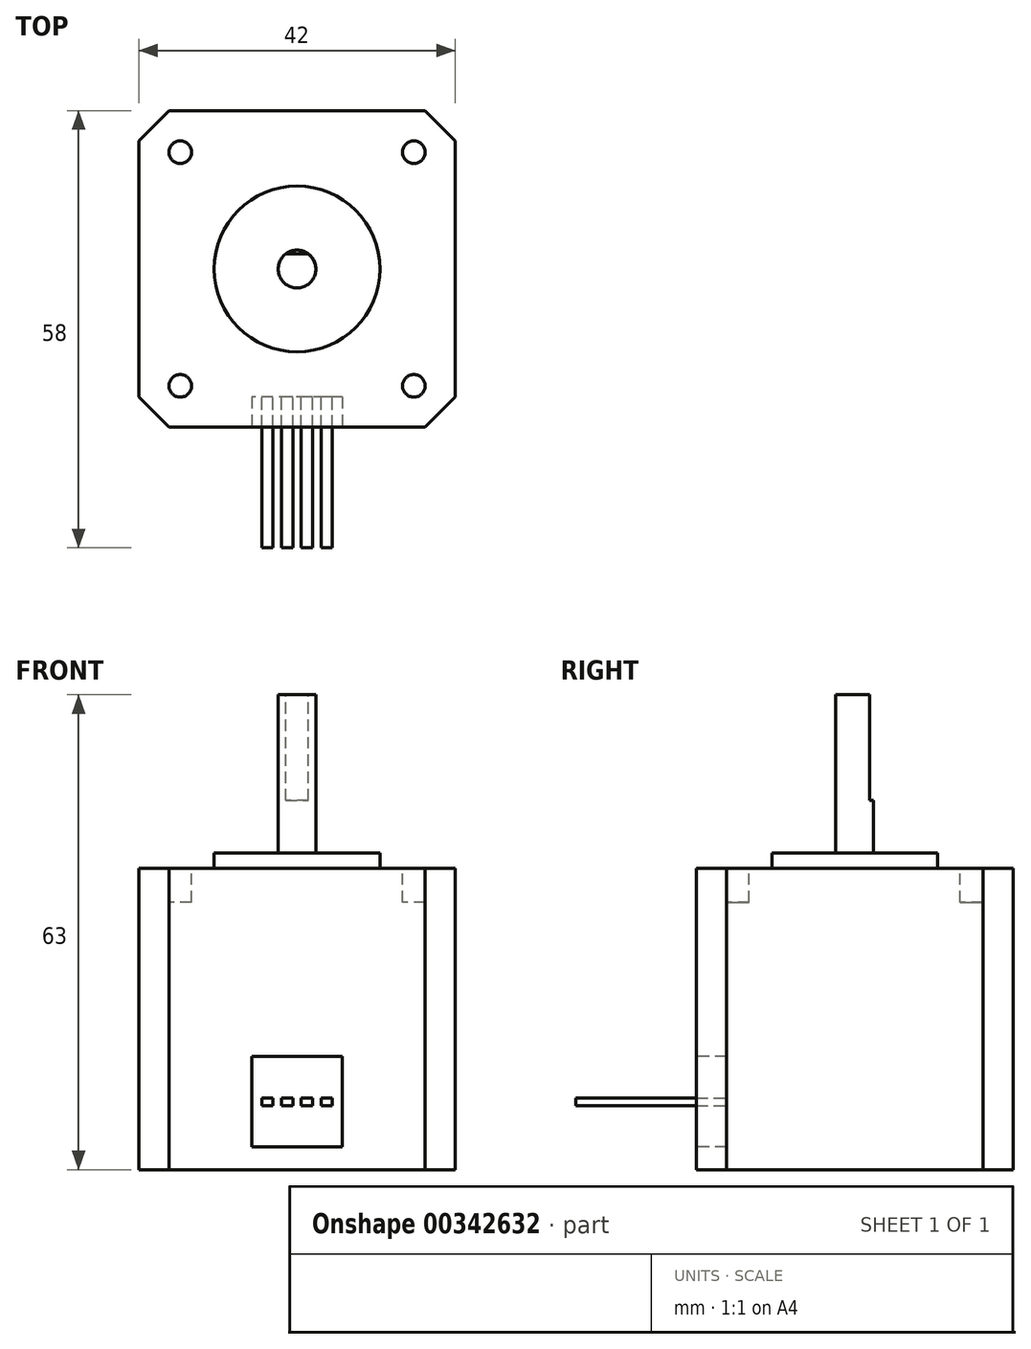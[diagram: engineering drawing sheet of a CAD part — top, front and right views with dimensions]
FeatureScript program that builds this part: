
annotation { "Feature Type Name" : "Feature", "Feature Type Description" : "" }
export const myFeature = defineFeature(function(context is Context, id is Id, definition is map)
    precondition{}
    {
        {
            var Q0;
            Q0=qCreatedBy(makeId("Top.planeOp"),FACE);
            var sketch = newSketch(context, id + "F0", { "sketchPlane" : qUnion([Q0])});
            skLineSegment(sketch, "E0.bottom", {"start": v(21, -21) * mm, "end": v(-21, -21) * mm});
            skLineSegment(sketch, "E0.top", {"start": v(21, 21) * mm, "end": v(-21, 21) * mm});
            skLineSegment(sketch, "E0.left", {"start": v(21, -21) * mm, "end": v(21, 21) * mm});
            skLineSegment(sketch, "E0.right", {"start": v(-21, -21) * mm, "end": v(-21, 21) * mm});
            skPoint(sketch, "E0.middle", {"position": v(0, 0) * mm});
            skSolve(sketch);
        }
        {
            var Q0;
            Q0=qSketchRegion(id+"F0",true);
            extrude(context, id + "F1", {"entities" : qUnion([Q0]), "depth" : 40 * mm});
        }
        {
            var Q0;
            Q0=makeQuery(id+"F1.opExtrude","CAP_FACE",FACE,{"disambiguationData":[OSD([sQuery(id+"F0.wireOp",EDGE,"E0.bottom"),sQuery(id+"F0.wireOp",EDGE,"E0.top"),sQuery(id+"F0.wireOp",EDGE,"E0.left"),sQuery(id+"F0.wireOp",EDGE,"E0.right")])],"isStart":false});
            var sketch = newSketch(context, id + "F2", { "sketchPlane" : qUnion([Q0])});
            skLineSegment(sketch, "E1", {"start": v(21, -21) * mm, "end": v(-21, 21) * mm, "construction": true});
            skLineSegment(sketch, "E2", {"start": v(-21, -21) * mm, "end": v(21, 21) * mm, "construction": true});
            skCircle(sketch, "E3", {"center": v(15.5, 15.5) * mm, "radius": 1.5 * mm});
            skCircle(sketch, "E4", {"center": v(15.5, -15.5) * mm, "radius": 1.5 * mm});
            skLineSegment(sketch, "E5", {"start": v(15.5, -15.5) * mm, "end": v(15.5, 15.5) * mm, "construction": true});
            skCircle(sketch, "E6.MirrorC", {"center": v(-15.5, -15.5) * mm, "radius": 1.5 * mm});
            skCircle(sketch, "E7.MirrorC", {"center": v(-15.5, 15.5) * mm, "radius": 1.5 * mm});
            skSolve(sketch);
        }
        {
            var Q0;
            Q0=qSketchRegion(id+"F2",true);
            extrude(context, id + "F3", {"entities" : qUnion([Q0]), "operationType" : NewBodyOperationType.REMOVE, "oppositeDirection" : true, "depth" : 4.5 * mm});
        }
        {
            var Q0;
            Q0=makeQuery(id+"F1.opExtrude","CAP_FACE",FACE,{"disambiguationData":[OSD([sQuery(id+"F0.wireOp",EDGE,"E0.bottom"),sQuery(id+"F0.wireOp",EDGE,"E0.top"),sQuery(id+"F0.wireOp",EDGE,"E0.left"),sQuery(id+"F0.wireOp",EDGE,"E0.right")])],"isStart":false});
            var sketch = newSketch(context, id + "F4", { "sketchPlane" : qUnion([Q0])});
            skLineSegment(sketch, "E8", {"start": v(21, 17) * mm, "end": v(17, 21) * mm});
            skLineSegment(sketch, "E9", {"start": v(15.5, 17) * mm, "end": v(33, 17) * mm, "construction": true});
            skLineSegment(sketch, "E10", {"start": v(21, 17) * mm, "end": v(21, 21) * mm});
            skLineSegment(sketch, "E11", {"start": v(21, 21) * mm, "end": v(17, 21) * mm});
            skLineSegment(sketch, "E12.MirrorCS", {"start": v(21, -21) * mm, "end": v(17, -21) * mm});
            skLineSegment(sketch, "E13.MirrorCS", {"start": v(21, -17) * mm, "end": v(21, -21) * mm});
            skLineSegment(sketch, "E14.MirrorCS", {"start": v(21, -17) * mm, "end": v(17, -21) * mm});
            skLineSegment(sketch, "E15.MirrorCS", {"start": v(-21, -17) * mm, "end": v(-17, -21) * mm});
            skLineSegment(sketch, "E16.MirrorCS", {"start": v(-21, -17) * mm, "end": v(-21, -21) * mm});
            skLineSegment(sketch, "E17.MirrorCS", {"start": v(-21, -21) * mm, "end": v(-17, -21) * mm});
            skLineSegment(sketch, "E18.MirrorCS", {"start": v(-21, 21) * mm, "end": v(-17, 21) * mm});
            skLineSegment(sketch, "E19.MirrorCS", {"start": v(-21, 17) * mm, "end": v(-17, 21) * mm});
            skLineSegment(sketch, "E20.MirrorCS", {"start": v(-21, 17) * mm, "end": v(-21, 21) * mm});
            skSolve(sketch);
        }
        {
            var Q0;
            Q0=qSketchRegion(id+"F4",true);
            extrude(context, id + "F5", {"entities" : qUnion([Q0]), "operationType" : NewBodyOperationType.REMOVE, "endBound" : BoundingType.THROUGH_ALL, "oppositeDirection" : true, "depth" : 25 * mm});
        }
        {
            var Q0;
            Q0=makeQuery(id+"F1.opExtrude","CAP_FACE",FACE,{"disambiguationData":[OSD([sQuery(id+"F0.wireOp",EDGE,"E0.bottom"),sQuery(id+"F0.wireOp",EDGE,"E0.top"),sQuery(id+"F0.wireOp",EDGE,"E0.left"),sQuery(id+"F0.wireOp",EDGE,"E0.right")])],"isStart":false});
            var sketch = newSketch(context, id + "F6", { "sketchPlane" : qUnion([Q0])});
            skCircle(sketch, "E21", {"center": v(0, 0) * mm, "radius": 11 * mm});
            skSolve(sketch);
        }
        {
            var Q0;
            Q0=qSketchRegion(id+"F6",true);
            extrude(context, id + "F7", {"entities" : qUnion([Q0]), "operationType" : NewBodyOperationType.ADD, "depth" : 2 * mm});
        }
        {
            var Q0;
            Q0=makeQuery(id+"F7.opExtrude","CAP_FACE",FACE,{"disambiguationData":[OSD([sQuery(id+"F6.wireOp",EDGE,"E21")])],"isStart":false});
            var sketch = newSketch(context, id + "F8", { "sketchPlane" : qUnion([Q0])});
            skCircle(sketch, "E22", {"center": v(0, 0) * mm, "radius": 2.5 * mm});
            skSolve(sketch);
        }
        {
            var Q0;
            Q0=qSketchRegion(id+"F8",true);
            extrude(context, id + "F9", {"entities" : qUnion([Q0]), "operationType" : NewBodyOperationType.ADD, "depth" : (23 - 2) * mm});
        }
        {
            var Q0;
            Q0=makeQuery(id+"F9.opExtrude","CAP_FACE",FACE,{"disambiguationData":[OSD([sQuery(id+"F8.wireOp",EDGE,"E22")])],"isStart":false});
            var sketch = newSketch(context, id + "F10", { "sketchPlane" : qUnion([Q0])});
            skArc(sketch, "E23.0", {"start": v(1.5, 2) * mm, "mid": v(0, 2.5) * mm, "end": v(-1.5, 2) * mm});
            skLineSegment(sketch, "E24", {"start": v(-1.5, 2) * mm, "end": v(1.5, 2) * mm});
            skSolve(sketch);
        }
        {
            var Q0;
            Q0=qSketchRegion(id+"F10",true);
            extrude(context, id + "F11", {"entities" : qUnion([Q0]), "operationType" : NewBodyOperationType.REMOVE, "oppositeDirection" : true, "depth" : 14 * mm});
        }
        {
            var Q0;
            Q0=makeQuery(id+"F1.opExtrude","SWEPT_FACE",FACE,{"disambiguationData":[OSD([sQuery(id+"F0.wireOp",EDGE,"E0.bottom")])]});
            var sketch = newSketch(context, id + "F12", { "sketchPlane" : qUnion([Q0])});
            skLineSegment(sketch, "E25.bottom", {"start": v(6, 3) * mm, "end": v(-6, 3) * mm});
            skLineSegment(sketch, "E25.top", {"start": v(6, 15) * mm, "end": v(-6, 15) * mm});
            skLineSegment(sketch, "E25.left", {"start": v(6, 3) * mm, "end": v(6, 15) * mm});
            skLineSegment(sketch, "E25.right", {"start": v(-6, 3) * mm, "end": v(-6, 15) * mm});
            skPoint(sketch, "E25.middle", {"position": v(0, 9) * mm});
            skSolve(sketch);
        }
        {
            var Q0;
            Q0=qSketchRegion(id+"F12",true);
            extrude(context, id + "F13", {"entities" : qUnion([Q0]), "operationType" : NewBodyOperationType.REMOVE, "oppositeDirection" : true, "depth" : 4 * mm});
        }
        {
            var Q0;
            Q0=makeQuery(id+"F13.boolean.opBoolean","COPY",FACE,{"derivedFrom":makeQuery(id+"F13.opExtrude","CAP_FACE",FACE,{"disambiguationData":[OSD([sQuery(id+"F12.wireOp",EDGE,"E25.bottom"),sQuery(id+"F12.wireOp",EDGE,"E25.top"),sQuery(id+"F12.wireOp",EDGE,"E25.left"),sQuery(id+"F12.wireOp",EDGE,"E25.right")])],"isStart":false})});
            var sketch = newSketch(context, id + "F14", { "sketchPlane" : qUnion([Q0])});
            skLineSegment(sketch, "E26", {"start": v(6, 9) * mm, "end": v(-6, 9) * mm, "construction": true});
            skLineSegment(sketch, "E27.bottom", {"start": v(-3.19, 8.5) * mm, "end": v(-4.69, 8.5) * mm});
            skLineSegment(sketch, "E27.top", {"start": v(-3.19, 9.5) * mm, "end": v(-4.69, 9.5) * mm});
            skLineSegment(sketch, "E27.left", {"start": v(-3.19, 8.5) * mm, "end": v(-3.19, 9.5) * mm});
            skLineSegment(sketch, "E27.right", {"start": v(-4.69, 8.5) * mm, "end": v(-4.69, 9.5) * mm});
            skPoint(sketch, "E27.middle", {"position": v(-3.94, 9) * mm});
            skPoint(sketch, "E28.1.0.0", {"position": v(-1.31, 9) * mm});
            skLineSegment(sketch, "E28.1.0.1", {"start": v(-2.06, 8.5) * mm, "end": v(-2.06, 9.5) * mm});
            skLineSegment(sketch, "E28.1.0.2", {"start": v(-0.56, 8.5) * mm, "end": v(-0.56, 9.5) * mm});
            skLineSegment(sketch, "E28.1.0.3", {"start": v(-0.56, 9.5) * mm, "end": v(-2.06, 9.5) * mm});
            skLineSegment(sketch, "E28.1.0.4", {"start": v(-0.56, 8.5) * mm, "end": v(-2.06, 8.5) * mm});
            skPoint(sketch, "E28.2.0.0", {"position": v(1.31, 9) * mm});
            skLineSegment(sketch, "E28.2.0.1", {"start": v(0.56, 8.5) * mm, "end": v(0.56, 9.5) * mm});
            skLineSegment(sketch, "E28.2.0.2", {"start": v(2.06, 8.5) * mm, "end": v(2.06, 9.5) * mm});
            skLineSegment(sketch, "E28.2.0.3", {"start": v(2.06, 9.5) * mm, "end": v(0.56, 9.5) * mm});
            skLineSegment(sketch, "E28.2.0.4", {"start": v(2.06, 8.5) * mm, "end": v(0.56, 8.5) * mm});
            skPoint(sketch, "E28.3.0.0", {"position": v(3.94, 9) * mm});
            skLineSegment(sketch, "E28.3.0.1", {"start": v(3.19, 8.5) * mm, "end": v(3.19, 9.5) * mm});
            skLineSegment(sketch, "E28.3.0.2", {"start": v(4.69, 8.5) * mm, "end": v(4.69, 9.5) * mm});
            skLineSegment(sketch, "E28.3.0.3", {"start": v(4.69, 9.5) * mm, "end": v(3.19, 9.5) * mm});
            skLineSegment(sketch, "E28.3.0.4", {"start": v(4.69, 8.5) * mm, "end": v(3.19, 8.5) * mm});
            skLineSegment(sketch, "E28.direction1", {"start": v(-3.94, 9) * mm, "end": v(-1.31, 9) * mm, "construction": true});
            skSolve(sketch);
        }
        {
            var Q0;
            Q0=qSketchRegion(id+"F14",true);
            extrude(context, id + "F15", {"entities" : qUnion([Q0]), "operationType" : NewBodyOperationType.ADD, "depth" : 20 * mm});
        }
    });
